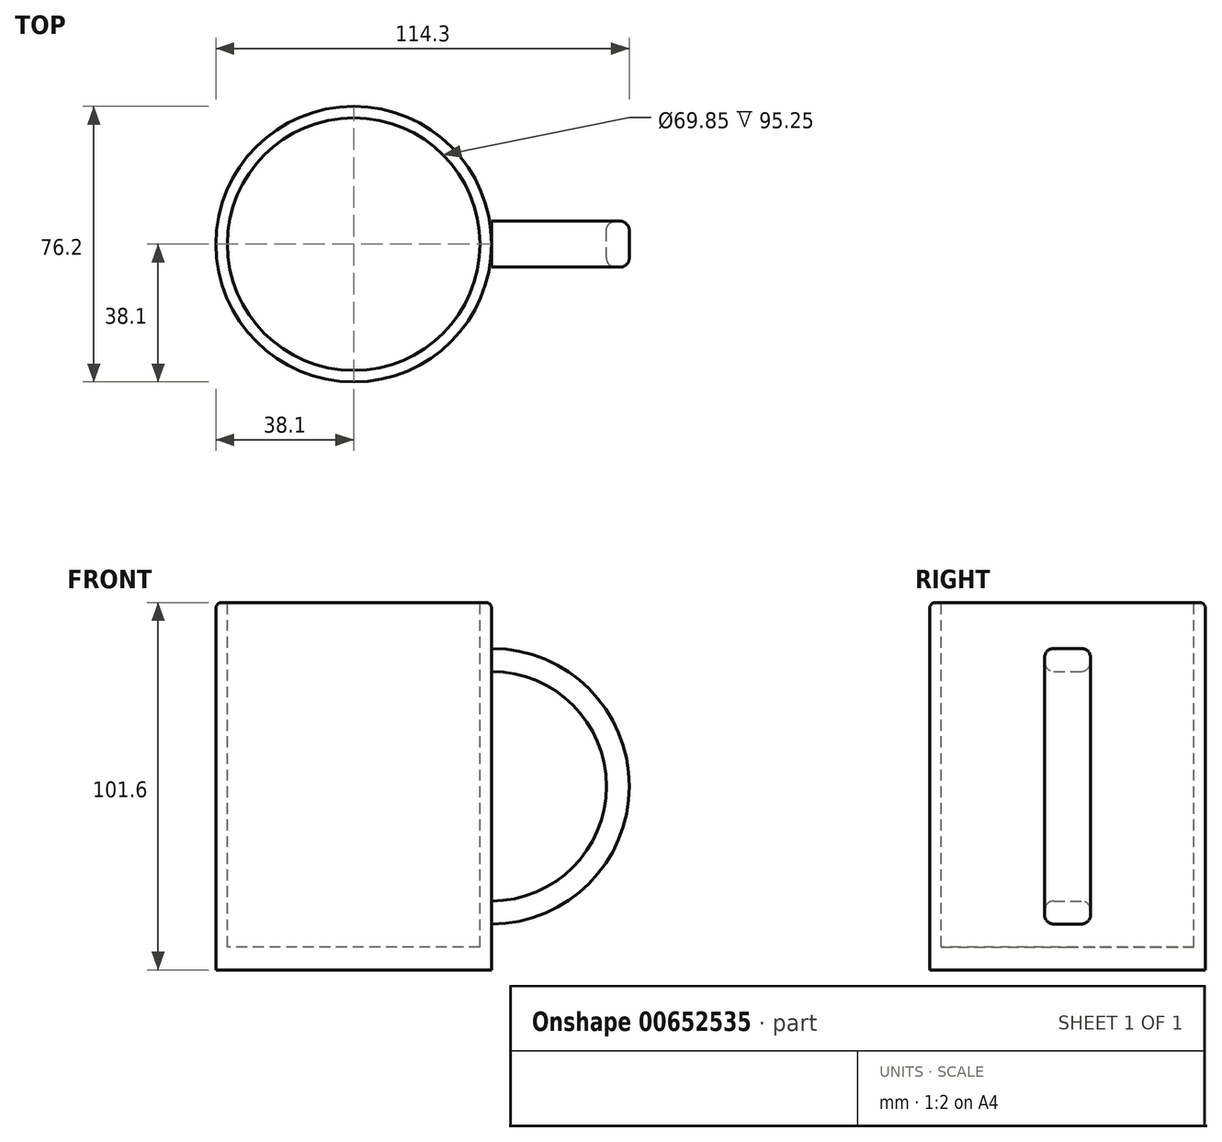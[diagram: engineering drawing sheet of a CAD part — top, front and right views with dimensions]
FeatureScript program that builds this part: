
annotation { "Feature Type Name" : "Feature", "Feature Type Description" : "" }
export const myFeature = defineFeature(function(context is Context, id is Id, definition is map)
    precondition{}
    {
        {
            var Q0;
            Q0=qCreatedBy(makeId("Top.planeOp"),FACE);
            var sketch = newSketch(context, id + "F0", { "sketchPlane" : qUnion([Q0])});
            skCircle(sketch, "E0", {"center": v(0, 0) * mm, "radius": 38.1 * mm});
            skSolve(sketch);
        }
        {
            var Q0;
            Q0 = qSketchRegion(id + "F0", true);
            extrude(context, id + "F1", {"entities" : qUnion([Q0]), "depth" : 50.8 * mm, "offsetDistance" : 25.4 * mm, "hasSecondDirection" : true, "secondDirectionOppositeDirection" : true, "secondDirectionDepth" : 50.8 * mm});
        }
        {
            var Q0;
            Q0=qCreatedBy(makeId("Front.planeOp"),FACE);
            var sketch = newSketch(context, id + "F2", { "sketchPlane" : qUnion([Q0])});
            skArc(sketch, "E1", {"start": v(38.1, -38.1) * mm, "mid": v(65.04, -26.94) * mm, "end": v(76.2, 0) * mm});
            skArc(sketch, "E2", {"start": v(76.2, 0) * mm, "mid": v(65.04, 26.94) * mm, "end": v(38.1, 38.1) * mm});
            skArc(sketch, "E3.0", {"start": v(38.1, -31.75) * mm, "mid": v(60.55, -22.45) * mm, "end": v(69.85, 0) * mm});
            skArc(sketch, "E4.0", {"start": v(69.85, 0) * mm, "mid": v(60.55, 22.45) * mm, "end": v(38.1, 31.75) * mm});
            skLineSegment(sketch, "E5", {"start": v(38.1, 38.1) * mm, "end": v(38.1, 31.75) * mm});
            skLineSegment(sketch, "E6", {"start": v(38.1, -31.75) * mm, "end": v(38.1, -38.1) * mm});
            skSolve(sketch);
        }
        {
            var Q0;
            Q0 = qSketchRegion(id + "F2", true);
            extrude(context, id + "F3", {"entities" : qUnion([Q0]), "depth" : 6.35 * mm, "offsetDistance" : 25.4 * mm, "hasSecondDirection" : true, "secondDirectionOppositeDirection" : true, "secondDirectionDepth" : 6.35 * mm});
        }
        {
            var Q0;
            Q0=makeQuery(id+"F3.opExtrude","CAP_EDGE",EDGE,{"disambiguationData":[OSD([sQuery(id+"F2.wireOp",EDGE,"E1"),sQuery(id+"F2.wireOp",EDGE,"E2")])],"isStart":false});
            var Q1;
            Q1=makeQuery(id+"F3.opExtrude","CAP_EDGE",EDGE,{"disambiguationData":[OSD([sQuery(id+"F2.wireOp",EDGE,"E3.0"),sQuery(id+"F2.wireOp",EDGE,"E4.0")])],"isStart":false});
            var Q2;
            Q2=makeQuery(id+"F3.opExtrude","CAP_EDGE",EDGE,{"disambiguationData":[OSD([sQuery(id+"F2.wireOp",EDGE,"E1"),sQuery(id+"F2.wireOp",EDGE,"E2")])],"isStart":true});
            var Q3;
            Q3=makeQuery(id+"F3.opExtrude","CAP_EDGE",EDGE,{"disambiguationData":[OSD([sQuery(id+"F2.wireOp",EDGE,"E3.0"),sQuery(id+"F2.wireOp",EDGE,"E4.0")])],"isStart":true});
            fillet(context, id + "F4", {"entities" : qUnion([Q0, Q1, Q2, Q3]), "radius" : 2.54 * mm, "tangentPropagation" : true, "allowEdgeOverflow" : false});
        }
        {
            var Q0;
            Q0=makeQuery(id+"F1.opExtrude","CAP_FACE",FACE,{"disambiguationData":[OSD([sQuery(id+"F0.wireOp",EDGE,"E0")])],"isStart":false});
            var sketch = newSketch(context, id + "F5", { "sketchPlane" : qUnion([Q0])});
            skCircle(sketch, "E7", {"center": v(0, 0) * mm, "radius": 34.93 * mm});
            skSolve(sketch);
        }
        {
            var Q0;
            Q0 = qSketchRegion(id + "F5", true);
            extrude(context, id + "F6", {"entities" : qUnion([Q0]), "operationType" : NewBodyOperationType.REMOVE, "oppositeDirection" : true, "depth" : 95.25 * mm, "offsetDistance" : 25.4 * mm});
        }
        {
            var Q0;
            Q0=makeQuery(id+"F1.opExtrude","CAP_EDGE",EDGE,{"disambiguationData":[OSD([sQuery(id+"F0.wireOp",EDGE,"E0")])],"isStart":false});
            var Q1;
            Q1=makeQuery(id+"F6.boolean.opBoolean","COPY",EDGE,{"derivedFrom":makeQuery(id+"F6.opExtrude","CAP_EDGE",EDGE,{"disambiguationData":[OSD([sQuery(id+"F5.wireOp",EDGE,"E7")])],"isStart":true})});
            fillet(context, id + "F7", {"entities" : qUnion([Q0, Q1]), "radius" : 1.59 * mm, "tangentPropagation" : true, "allowEdgeOverflow" : false});
        }
    });
